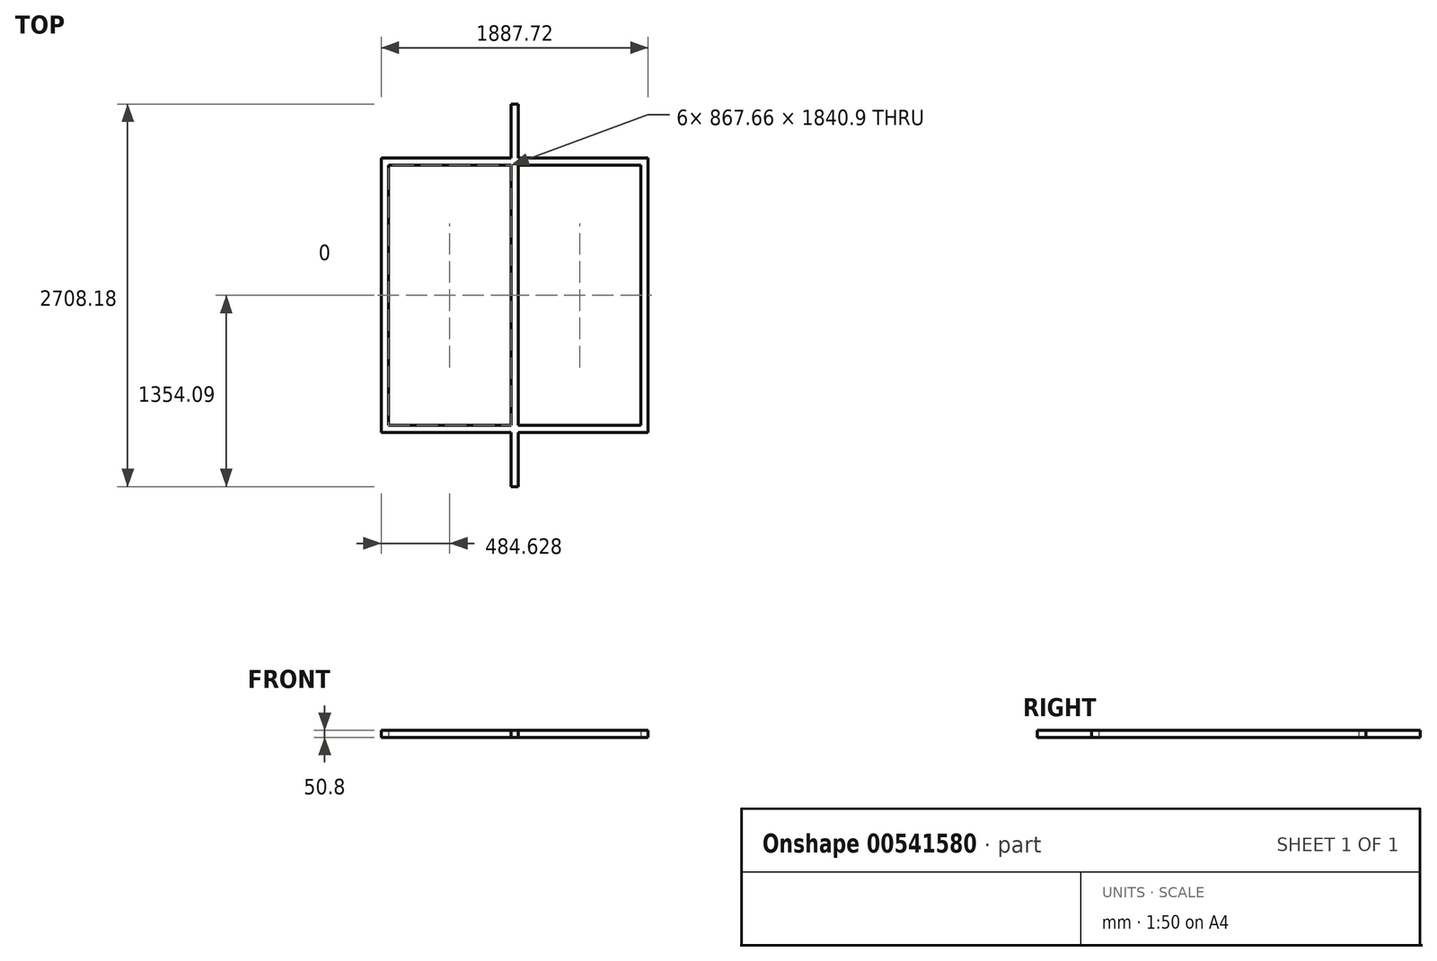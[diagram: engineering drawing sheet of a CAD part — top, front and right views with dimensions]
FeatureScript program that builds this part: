
annotation { "Feature Type Name" : "Feature", "Feature Type Description" : "" }
export const myFeature = defineFeature(function(context is Context, id is Id, definition is map)
    precondition{}
    {
        {
            var Q0;
            Q0=qCreatedBy(makeId("Top.planeOp"),FACE);
            var sketch = newSketch(context, id + "F0", { "sketchPlane" : qUnion([Q0])});
            skCircle(sketch, "E0", {"center": v(0, 0) * mm, "radius": 1354.33 * mm, "construction": true});
            skLineSegment(sketch, "E1.bottom", {"start": v(-943.86, 971.25) * mm, "end": v(-893.06, 971.25) * mm});
            skLineSegment(sketch, "E1.top", {"start": v(-943.86, -971.25) * mm, "end": v(-893.06, -971.25) * mm});
            skLineSegment(sketch, "E1.left", {"start": v(-943.86, 971.25) * mm, "end": v(-943.86, -971.25) * mm});
            skLineSegment(sketch, "E1.right", {"start": v(-893.06, 920.45) * mm, "end": v(-893.06, -920.45) * mm});
            skLineSegment(sketch, "E2.bottom", {"start": v(893.06, 971.25) * mm, "end": v(943.86, 971.25) * mm});
            skLineSegment(sketch, "E2.top", {"start": v(893.06, -971.25) * mm, "end": v(943.86, -971.25) * mm});
            skLineSegment(sketch, "E2.left", {"start": v(893.06, 920.45) * mm, "end": v(893.06, -920.45) * mm});
            skLineSegment(sketch, "E2.right", {"start": v(943.86, 971.25) * mm, "end": v(943.86, -971.25) * mm});
            skLineSegment(sketch, "E3", {"start": v(0, 0) * mm, "end": v(0, 1354.33) * mm, "construction": true});
            skLineSegment(sketch, "E4.bottom", {"start": v(-25.4, 1354.09) * mm, "end": v(25.4, 1354.09) * mm});
            skLineSegment(sketch, "E4.top", {"start": v(-25.4, -1354.09) * mm, "end": v(25.4, -1354.09) * mm});
            skLineSegment(sketch, "E4.left", {"start": v(-25.4, 1354.09) * mm, "end": v(-25.4, 971.25) * mm});
            skLineSegment(sketch, "E4.right", {"start": v(25.4, 1354.09) * mm, "end": v(25.4, 971.25) * mm});
            skLineSegment(sketch, "E5", {"start": v(0, 1354.09) * mm, "end": v(0, -1354.09) * mm, "construction": true});
            skLineSegment(sketch, "E6", {"start": v(-893.06, -971.25) * mm, "end": v(-25.4, -971.25) * mm});
            skLineSegment(sketch, "E7", {"start": v(893.06, -920.45) * mm, "end": v(25.4, -920.45) * mm});
            skLineSegment(sketch, "E8.trimOffspring", {"start": v(25.4, -971.25) * mm, "end": v(25.4, -1354.09) * mm});
            skLineSegment(sketch, "E9.trimOffspring", {"start": v(-25.4, -920.45) * mm, "end": v(-893.06, -920.45) * mm});
            skLineSegment(sketch, "E10.trimOffspring", {"start": v(-25.4, -971.25) * mm, "end": v(-25.4, -1354.09) * mm});
            skLineSegment(sketch, "E11.trimOffspring", {"start": v(25.4, -971.25) * mm, "end": v(893.06, -971.25) * mm});
            skLineSegment(sketch, "E12", {"start": v(-893.06, 971.25) * mm, "end": v(-25.4, 971.25) * mm});
            skLineSegment(sketch, "E13", {"start": v(-893.06, 920.45) * mm, "end": v(-25.4, 920.45) * mm});
            skLineSegment(sketch, "E14.trimOffspring", {"start": v(25.4, 920.45) * mm, "end": v(25.4, -920.45) * mm});
            skLineSegment(sketch, "E15.trimOffspring", {"start": v(-25.4, 920.45) * mm, "end": v(-25.4, -920.45) * mm});
            skLineSegment(sketch, "E16.trimOffspring", {"start": v(25.4, 971.25) * mm, "end": v(893.06, 971.25) * mm});
            skLineSegment(sketch, "E17.trimOffspring", {"start": v(25.4, 920.45) * mm, "end": v(893.06, 920.45) * mm});
            skSolve(sketch);
        }
        {
            var Q0;
            Q0 = qSketchRegion(id + "F0", true);
            extrude(context, id + "F1", {"entities" : qUnion([Q0]), "depth" : 50.8 * mm, "offsetDistance" : 25.4 * mm});
        }
    });
